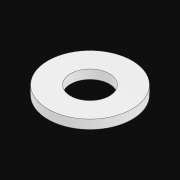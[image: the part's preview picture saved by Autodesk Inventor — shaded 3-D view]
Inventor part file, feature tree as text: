
AUTODESK INVENTOR PART (.ipt)
format: ipt  version: 2021.3 (Build 253353010, 353A)  size: 98,304 bytes
history: native  units: in
note: dims shown in document units (in); Inventor stores cm internally (conversion verified against a paired STEP export)
features: other x5, extrude x1, sketch x1
ambient origin geometry x8: Origin, YZ Plane, XZ Plane, XY Plane, X Axis, Y Axis, Z Axis, Center Point
bodies: Solid1 (feature_tree)
feature tree (7):
  other  "Table"
  other  "TWasher .375 OD x .04000"
  other  "TWasher .375 OD x .06250"
  other  "TWasher .375 OD x .03125"
  other  "TWasher .500 OD x .04000"
  extrude  "Extrusion1"  Depth=0.375in
  sketch  "Sketch1"  dims[d0=0.173in d1=0.375in d3=0.0in]
